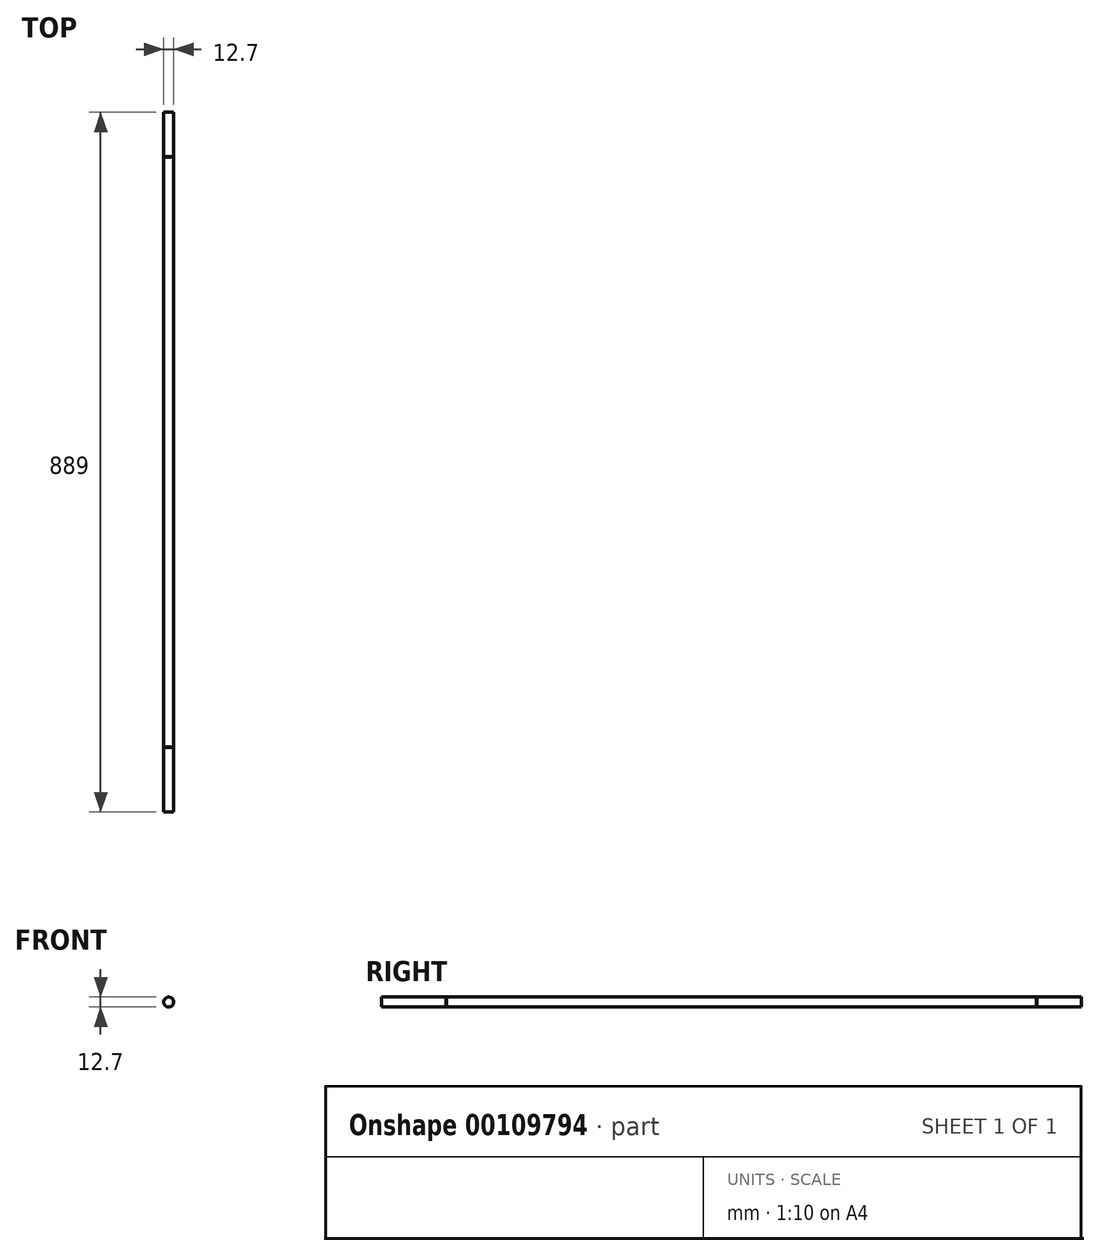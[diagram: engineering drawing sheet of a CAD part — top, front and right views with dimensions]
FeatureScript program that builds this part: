
annotation { "Feature Type Name" : "Feature", "Feature Type Description" : "" }
export const myFeature = defineFeature(function(context is Context, id is Id, definition is map)
    precondition{}
    {
        {
            var Q0;
            Q0=qCreatedBy(makeId("Front.planeOp"),FACE);
            var sketch = newSketch(context, id + "F0", { "sketchPlane" : qUnion([Q0])});
            skCircle(sketch, "E0", {"center": v(0, 0) * mm, "radius": 6.35 * mm});
            skSolve(sketch);
        }
        {
            var Q0;
            Q0 = qSketchRegion(id + "F0", true);
            extrude(context, id + "F1", {"entities" : qUnion([Q0]), "depth" : 889 * mm});
        }
        {
            var Q0;
            Q0=qCreatedBy(makeId("Right.planeOp"),FACE);
            var sketch = newSketch(context, id + "F2", { "sketchPlane" : qUnion([Q0])});
            skLineSegment(sketch, "E1.right", {"start": v(-806.45, 6.53) * mm, "end": v(-806.45, 5.28) * mm});
            skPoint(sketch, "E2.oppositeSnap0", {"position": v(-722.03, 5.28) * mm});
            skLineSegment(sketch, "E2.bottom", {"start": v(-806.89, 5.28) * mm, "end": v(-806.45, 5.28) * mm});
            skLineSegment(sketch, "E3", {"start": v(-806.89, 5.28) * mm, "end": v(-806.89, 6.54) * mm});
            skLineSegment(sketch, "E4", {"start": v(-806.89, 6.54) * mm, "end": v(-806.45, 6.53) * mm});
            skSolve(sketch);
        }
        {
            var Q0;
            Q0 = qSketchRegion(id + "F2", true);
            var Q1;
            Q1=makeQuery(id+"F1.opExtrude","CAP_EDGE",EDGE,{"disambiguationData":[OSD([sQuery(id+"F0.wireOp",EDGE,"E0")])],"isStart":false});
            sweep(context, id + "F3", {"profiles" : qUnion([Q0]), "path" : qUnion([Q1])});
        }
        {
            var Q0;
            Q0=makeQuery(id+"F3.opSweep","SWEPT_BODY",BODY,{"disambiguationData":[OSD([sQuery(id+"F0.wireOp",EDGE,"E0"),sQuery(id+"F2.wireOp",EDGE,"E1.right"),sQuery(id+"F2.wireOp",EDGE,"E2.bottom"),sQuery(id+"F2.wireOp",EDGE,"E3"),sQuery(id+"F2.wireOp",EDGE,"E4")])]});
            transform(context, id + "F4", {"entities" : qUnion([Q0]), "transformType" : TransformType.TRANSLATION_3D, "dx" : 0 * mm, "dy" : 750.06 * mm, "dz" : 0 * mm, "makeCopy" : true});
        }
        {
            var Q0;
            Q0=makeQuery(id+"F3.opSweep","SWEPT_BODY",BODY,{"disambiguationData":[OSD([sQuery(id+"F0.wireOp",EDGE,"E0"),sQuery(id+"F2.wireOp",EDGE,"E1.right"),sQuery(id+"F2.wireOp",EDGE,"E2.bottom"),sQuery(id+"F2.wireOp",EDGE,"E3"),sQuery(id+"F2.wireOp",EDGE,"E4")])]});
            var Q1;
            Q1=makeQuery(id+"F4.opPattern","COPY",BODY,{"derivedFrom":makeQuery(id+"F3.opSweep","SWEPT_BODY",BODY,{"disambiguationData":[OSD([sQuery(id+"F0.wireOp",EDGE,"E0"),sQuery(id+"F2.wireOp",EDGE,"E1.right"),sQuery(id+"F2.wireOp",EDGE,"E2.bottom"),sQuery(id+"F2.wireOp",EDGE,"E3"),sQuery(id+"F2.wireOp",EDGE,"E4")])]}),"instanceName":"1"});
            var Q2;
            Q2=makeQuery(id+"F1.opExtrude","SWEPT_BODY",BODY,{"disambiguationData":[OSD([sQuery(id+"F0.wireOp",EDGE,"E0")])]});
            booleanBodies(context, id + "F5", {"operationType" : BooleanOperationType.SUBTRACTION, "tools" : qUnion([Q0, Q1]), "targets" : qUnion([Q2])});
        }
    });
